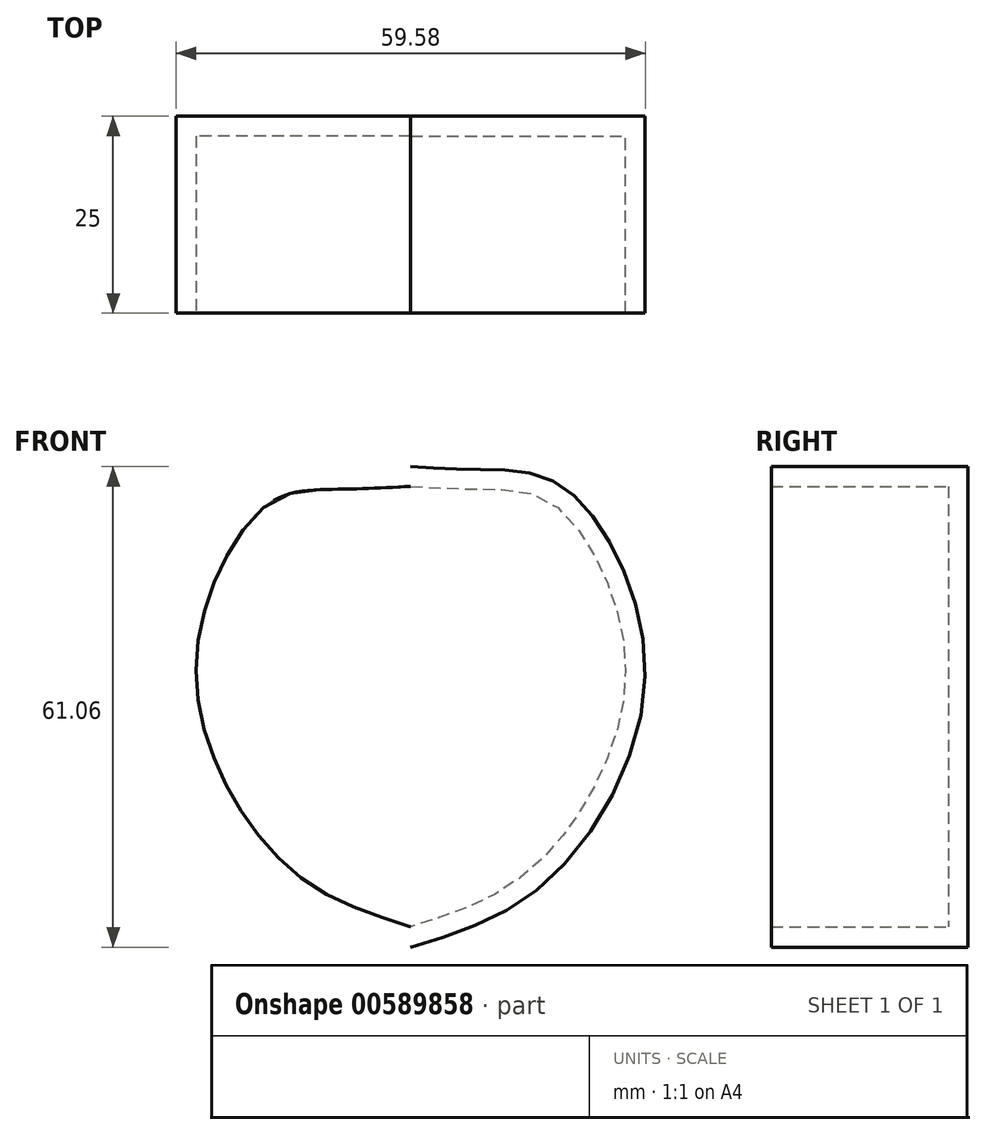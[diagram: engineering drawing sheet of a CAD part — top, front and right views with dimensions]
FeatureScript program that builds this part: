
annotation { "Feature Type Name" : "Feature", "Feature Type Description" : "" }
export const myFeature = defineFeature(function(context is Context, id is Id, definition is map)
    precondition{}
    {
        {
            var Q0;
            Q0=qCreatedBy(makeId("Front.planeOp"),FACE);
            var sketch = newSketch(context, id + "F0", { "sketchPlane" : qUnion([Q0])});
            skFitSpline(sketch, "E0", {"points": [v(0, 61.06) * mm, v(8.44, 60.7) * mm, v(17.7, 59.43) * mm, v(25.86, 50.35) * mm, v(29.49, 30.94) * mm, v(16.97, 8.07) * mm, v(0, 0) * mm], "startDerivative": vector(66.25, -3.89) * mm, "endDerivative": vector(-95.05, -28.69) * mm});
            skFitSpline(sketch, "E1.MirrorCS", {"points": [v(0, 61.06) * mm, v(-8.44, 60.7) * mm, v(-17.7, 59.43) * mm, v(-25.86, 50.35) * mm, v(-29.49, 30.94) * mm, v(-16.97, 8.07) * mm, v(0, 0) * mm], "startDerivative": vector(-66.25, -3.89) * mm, "endDerivative": vector(95.05, -28.69) * mm});
            skSolve(sketch);
        }
        {
            var Q0;
            Q0=makeQuery(id+"F0.imprint","IMPRINT",FACE,{"disambiguationData":[TD([[makeQuery(id+"F0.imprint","IMPRINT",EDGE,{"derivedFrom":sQuery(id+"F0.wireOp",EDGE,"E0")}),-1.0]])]});
            extrude(context, id + "F1", {"entities" : qUnion([Q0]), "depth" : 25 * mm, "offsetDistance" : 25 * mm});
        }
        {
            var Q0;
            Q0=makeQuery(id+"F1.opExtrude","CAP_FACE",FACE,{"disambiguationData":[OSD([sQuery(id+"F0.wireOp",EDGE,"E0"),sQuery(id+"F0.wireOp",EDGE,"E1.MirrorCS")])],"isStart":false});
            shell(context, id + "F2", {"entities" : qUnion([Q0]), "thickness" : 2.5 * mm});
        }
    });
